# Revit family: LIGHTGLASS V2 Standalone
name_source: partatom
category: Lighting Fixtures
units: mm (PartAtom-declared; Revit-internal decimal feet)

## family parameters
Cut with Voids When Loaded = Yes
Host = Face
Light Source = No
Part Type = Normal
Room Calculation Point = No
Round Connector Dimension = Use Diameter
Shared = No

## types (4) — shared parameters
Default Elevation = 4' - 0"
Description = AREA OF UNIT CANNOT NOT EXCEED 24 SQUARE FEET
URL = WWW.LIGHTGLASSLIGHTING.COM

## per-type parameters (varying)
| type | Depth from Face of Finish | Frame Width | Max Depth | Max Height | Max Width | Unit Height | Unit Width |
| LIGHTGLASS - SA - 1in Frame - 12x12 (Min Size) | 0' - 0 3/8" | 0' - 1" | 0' - 0 3/8" | 1' - 0" | 1' - 0" | 1' - 0" | 1' - 0" |
| LIGHTGLASS - SA - 1in Frame - 72x48 (Max Size) | 0' - 1" | 0' - 1" | 0' - 1" | 6' - 0" | 3' - 6" | 6' - 0" | 3' - 6" |
| LIGHTGLASS - SA - 2in Frame - 12x12 (Min Size) | 0' - 0 3/8" | 0' - 2" | 0' - 0 3/8" | 1' - 0" | 1' - 0" | 1' - 0" | 1' - 0" |
| LIGHTGLASS - SA - 2in Frame - 72x48 (Max Size) | 0' - 1" | 0' - 2" | 0' - 1" | 6' - 0" | 3' - 6" | 6' - 0" | 3' - 6" |

## geometry (parser evidence)
native form markers: Sweep x30
no freeform markers — native parametric forms only
